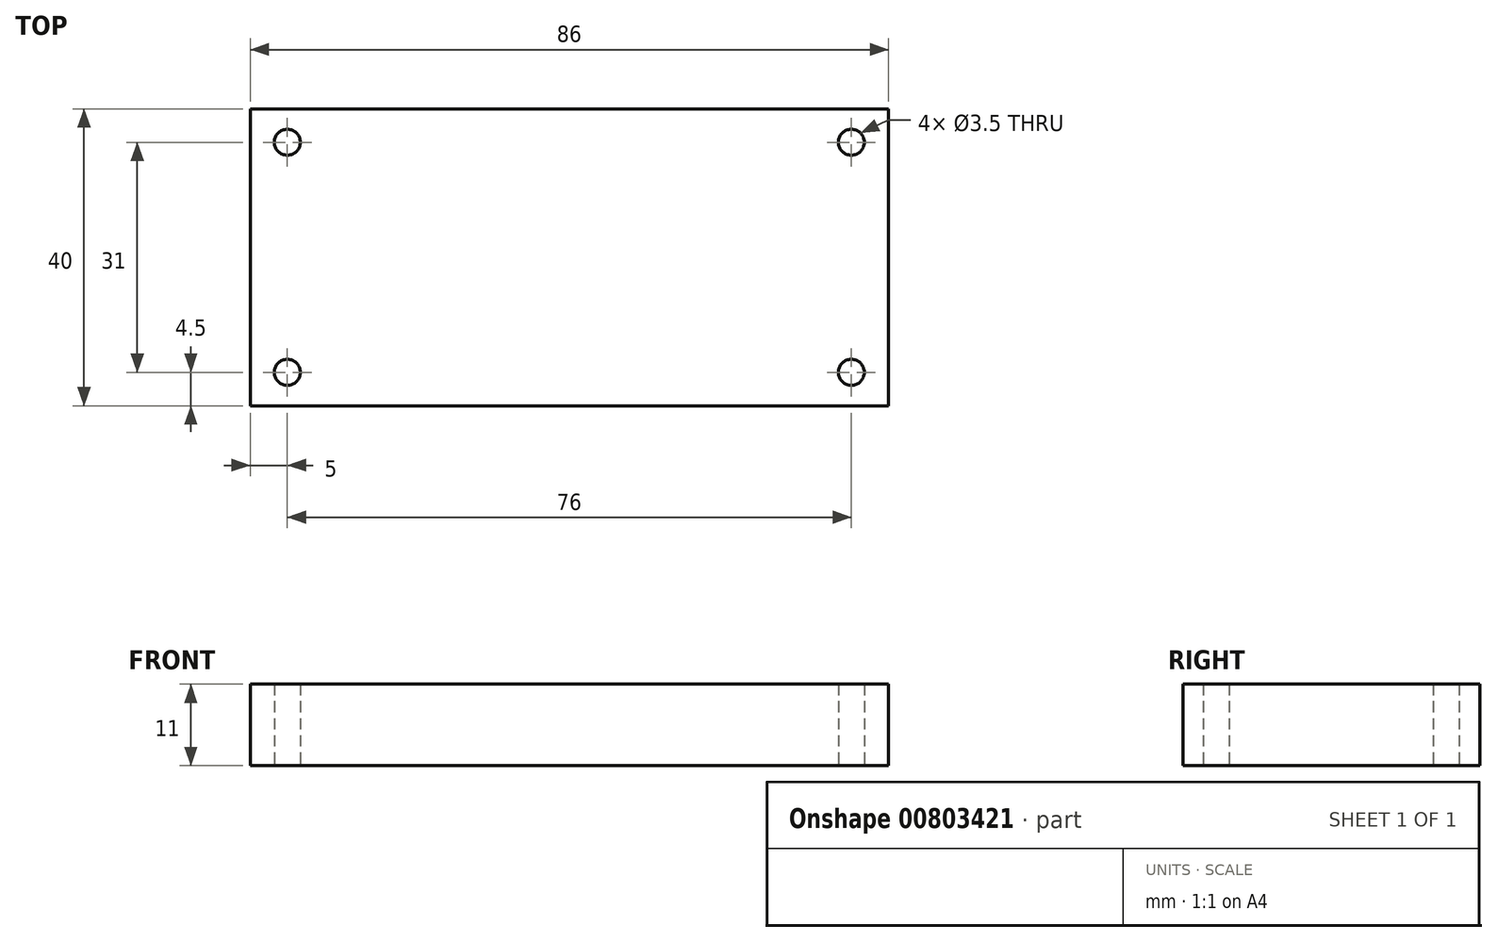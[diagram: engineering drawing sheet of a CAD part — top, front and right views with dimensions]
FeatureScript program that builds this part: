
annotation { "Feature Type Name" : "Feature", "Feature Type Description" : "" }
export const myFeature = defineFeature(function(context is Context, id is Id, definition is map)
    precondition{}
    {
        {
            var Q0;
            Q0=qCreatedBy(makeId("Top.planeOp"),FACE);
            var sketch = newSketch(context, id + "F0", { "sketchPlane" : qUnion([Q0])});
            skLineSegment(sketch, "E0.bottom", {"start": v(0, 40) * mm, "end": v(86, 40) * mm});
            skLineSegment(sketch, "E0.top", {"start": v(0, 0) * mm, "end": v(86, 0) * mm});
            skLineSegment(sketch, "E0.left", {"start": v(0, 40) * mm, "end": v(0, 0) * mm});
            skLineSegment(sketch, "E0.right", {"start": v(86, 40) * mm, "end": v(86, 0) * mm});
            skCircle(sketch, "E1", {"center": v(5, 35.5) * mm, "radius": 1.75 * mm});
            skCircle(sketch, "E2", {"center": v(5, 4.5) * mm, "radius": 1.75 * mm});
            skCircle(sketch, "E3", {"center": v(81, 4.5) * mm, "radius": 1.75 * mm});
            skCircle(sketch, "E4", {"center": v(81, 35.5) * mm, "radius": 1.75 * mm});
            skSolve(sketch);
        }
        {
            var Q0;
            Q0 = qSketchRegion(id + "F0", true);
            extrude(context, id + "F1", {"entities" : qUnion([Q0]), "depth" : 11 * mm, "offsetDistance" : 25 * mm});
        }
    });
